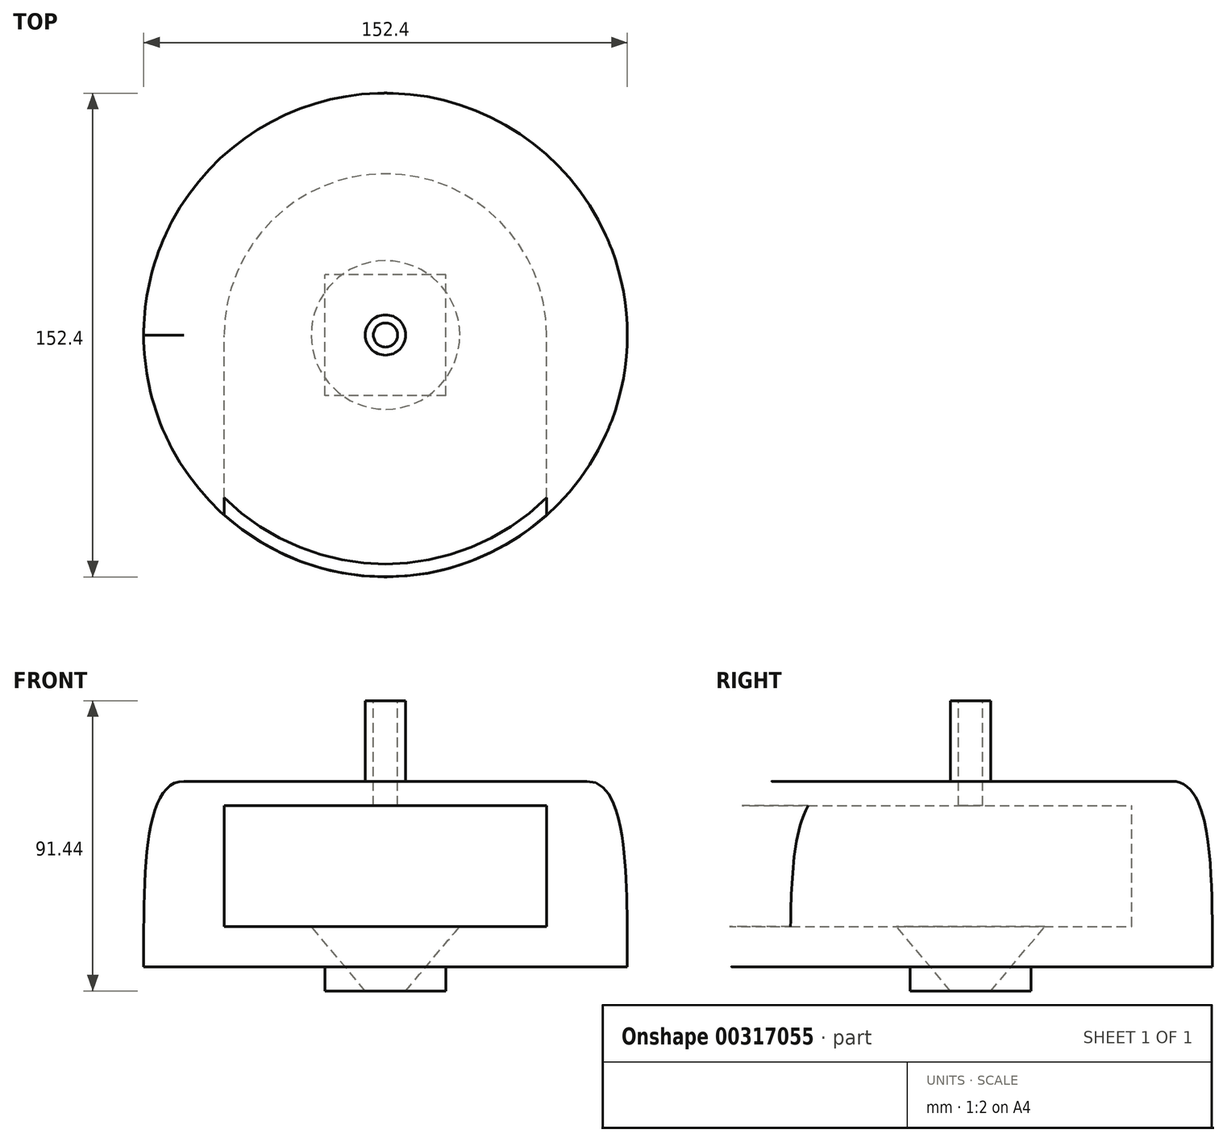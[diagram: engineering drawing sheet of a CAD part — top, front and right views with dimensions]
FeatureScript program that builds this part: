
annotation { "Feature Type Name" : "Feature", "Feature Type Description" : "" }
export const myFeature = defineFeature(function(context is Context, id is Id, definition is map)
    precondition{}
    {
        {
            var Q0;
            Q0=qCreatedBy(makeId("Front.planeOp"),FACE);
            var sketch = newSketch(context, id + "F0", { "sketchPlane" : qUnion([Q0])});
            skLineSegment(sketch, "E0", {"start": v(76.2, 0) * mm, "end": v(0, 0) * mm});
            skLineSegment(sketch, "E1", {"start": v(0, 0) * mm, "end": v(0, 58.42) * mm});
            skLineSegment(sketch, "E2", {"start": v(0, 58.42) * mm, "end": v(63.5, 58.42) * mm});
            skFitSpline(sketch, "E3", {"points": [v(76.2, 0) * mm, v(63.5, 58.42) * mm], "startDerivative": vector(0, 91.36) * mm, "endDerivative": vector(-38.1, 0) * mm});
            skSolve(sketch);
        }
        {
            var Q0;
            Q0 = qSketchRegion(id + "F0", true);
            var Q1;
            Q1=sQuery(id+"F0.wireOp",EDGE,"E1");
            revolve(context, id + "F1", {"entities" : qUnion([Q0]), "axis" : qUnion([Q1]), "revolveType" : RevolveType.FULL});
        }
        {
            var Q0;
            Q0=qCreatedBy(makeId("Front.planeOp"),FACE);
            var sketch = newSketch(context, id + "F2", { "sketchPlane" : qUnion([Q0])});
            skLineSegment(sketch, "E4.bottom", {"start": v(0, 12.7) * mm, "end": v(50.8, 12.7) * mm});
            skLineSegment(sketch, "E4.top", {"start": v(0, 50.8) * mm, "end": v(50.8, 50.8) * mm});
            skLineSegment(sketch, "E4.left", {"start": v(0, 12.7) * mm, "end": v(0, 50.8) * mm});
            skLineSegment(sketch, "E4.right", {"start": v(50.8, 12.7) * mm, "end": v(50.8, 50.8) * mm});
            skSolve(sketch);
        }
        {
            var Q0;
            Q0 = qSketchRegion(id + "F2", true);
            var Q1;
            Q1=sQuery(id+"F2.wireOp",EDGE,"E4.left");
            revolve(context, id + "F3", {"operationType" : NewBodyOperationType.REMOVE, "entities" : qUnion([Q0]), "axis" : qUnion([Q1]), "revolveType" : RevolveType.FULL, "oppositeDirection" : true});
        }
        {
            var Q0;
            Q0=qCreatedBy(makeId("Front.planeOp"),FACE);
            var sketch = newSketch(context, id + "F4", { "sketchPlane" : qUnion([Q0])});
            skLineSegment(sketch, "E5", {"start": v(0, -16.43) * mm, "end": v(0, 79.93) * mm, "construction": true});
            skLineSegment(sketch, "E6.bottom", {"start": v(50.8, 50.8) * mm, "end": v(-50.8, 50.8) * mm});
            skLineSegment(sketch, "E6.top", {"start": v(50.8, 12.7) * mm, "end": v(-50.8, 12.7) * mm});
            skLineSegment(sketch, "E6.left", {"start": v(50.8, 50.8) * mm, "end": v(50.8, 12.7) * mm});
            skLineSegment(sketch, "E6.right", {"start": v(-50.8, 50.8) * mm, "end": v(-50.8, 12.7) * mm});
            skPoint(sketch, "E6.middle", {"position": v(0, 31.75) * mm});
            skSolve(sketch);
        }
        {
            var Q0;
            Q0 = qSketchRegion(id + "F4", true);
            extrude(context, id + "F5", {"entities" : qUnion([Q0]), "operationType" : NewBodyOperationType.REMOVE, "endBound" : BoundingType.THROUGH_ALL, "depth" : 25.4 * mm});
        }
        {
            var Q0;
            Q0=makeQuery(id+"F1.opRevolve","SWEPT_FACE",FACE,{"disambiguationData":[OSD([sQuery(id+"F0.wireOp",EDGE,"E0")])]});
            var sketch = newSketch(context, id + "F6", { "sketchPlane" : qUnion([Q0])});
            skLineSegment(sketch, "E7.bottom", {"start": v(19.05, 19.05) * mm, "end": v(-19.05, 19.05) * mm});
            skLineSegment(sketch, "E7.top", {"start": v(19.05, -19.05) * mm, "end": v(-19.05, -19.05) * mm});
            skLineSegment(sketch, "E7.left", {"start": v(19.05, 19.05) * mm, "end": v(19.05, -19.05) * mm});
            skLineSegment(sketch, "E7.right", {"start": v(-19.05, 19.05) * mm, "end": v(-19.05, -19.05) * mm});
            skPoint(sketch, "E7.middle", {"position": v(0, 0) * mm});
            skSolve(sketch);
        }
        {
            var Q0;
            Q0 = qSketchRegion(id + "F6", true);
            extrude(context, id + "F7", {"entities" : qUnion([Q0]), "operationType" : NewBodyOperationType.ADD, "depth" : 7.62 * mm});
        }
        {
            var Q0;
            Q0=makeQuery(id+"F7.opExtrude","CAP_FACE",FACE,{"disambiguationData":[OSD([sQuery(id+"F6.wireOp",EDGE,"E7.bottom"),sQuery(id+"F6.wireOp",EDGE,"E7.top"),sQuery(id+"F6.wireOp",EDGE,"E7.left"),sQuery(id+"F6.wireOp",EDGE,"E7.right")])],"isStart":false});
            var sketch = newSketch(context, id + "F8", { "sketchPlane" : qUnion([Q0])});
            skCircle(sketch, "E8", {"center": v(0, 0) * mm, "radius": 6.35 * mm});
            skSolve(sketch);
        }
        {
            var Q0;
            Q0 = qSketchRegion(id + "F8", true);
            var Q1;
            Q1=makeQuery(id+"F5.boolean.opBoolean","MERGE",FACE,{"derivedFrom":[makeQuery(id+"F3.boolean.opBoolean","COPY",FACE,{"derivedFrom":makeQuery(id+"F3.opRevolve","SWEPT_FACE",FACE,{"disambiguationData":[OSD([sQuery(id+"F2.wireOp",EDGE,"E4.bottom")])]})}),makeQuery(id+"F5.opExtrude","SWEPT_FACE",FACE,{"disambiguationData":[OSD([sQuery(id+"F4.wireOp",EDGE,"E6.top")])]})]});
            extrude(context, id + "F9", {"entities" : qUnion([Q0]), "operationType" : NewBodyOperationType.REMOVE, "endBound" : BoundingType.UP_TO_SURFACE, "oppositeDirection" : true, "endBoundEntityFace" : qUnion([Q1]), "depth" : 25.4 * mm, "hasDraft" : true, "draftAngle" : 40 * degree});
        }
        {
            var Q0;
            Q0=makeQuery(id+"F1.opRevolve","SWEPT_FACE",FACE,{"disambiguationData":[OSD([sQuery(id+"F0.wireOp",EDGE,"E2")])]});
            var sketch = newSketch(context, id + "F10", { "sketchPlane" : qUnion([Q0])});
            skCircle(sketch, "E9", {"center": v(0, 0) * mm, "radius": 6.35 * mm});
            skSolve(sketch);
        }
        {
            var Q0;
            Q0 = qSketchRegion(id + "F10", true);
            extrude(context, id + "F11", {"entities" : qUnion([Q0]), "operationType" : NewBodyOperationType.ADD, "depth" : 25.4 * mm});
        }
        {
            var Q0;
            Q0=makeQuery(id+"F11.opExtrude","CAP_FACE",FACE,{"disambiguationData":[OSD([sQuery(id+"F10.wireOp",EDGE,"E9")])],"isStart":false});
            var sketch = newSketch(context, id + "F12", { "sketchPlane" : qUnion([Q0])});
            skCircle(sketch, "E10", {"center": v(0, 0) * mm, "radius": 3.81 * mm});
            skSolve(sketch);
        }
        {
            var Q0;
            Q0 = qSketchRegion(id + "F12", true);
            extrude(context, id + "F13", {"entities" : qUnion([Q0]), "operationType" : NewBodyOperationType.REMOVE, "endBound" : BoundingType.UP_TO_NEXT, "oppositeDirection" : true, "depth" : 25.4 * mm});
        }
    });
